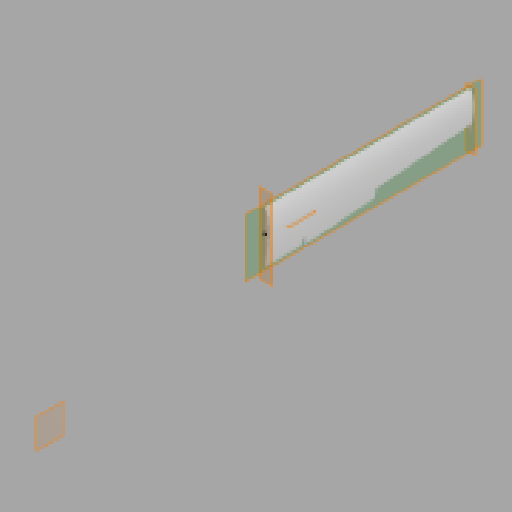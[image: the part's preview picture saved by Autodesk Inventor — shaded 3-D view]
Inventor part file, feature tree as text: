
AUTODESK INVENTOR PART (.ipt)
format: ipt  version: 2025 (Build 290162000, 162)  size: 286,208 bytes
history: native  units: in
note: dims shown in document units (in); Inventor stores cm internally (conversion verified against a paired STEP export)
features: other x7, plane x6, sketch x4
ambient origin geometry x8: Origin, YZ Plane, XZ Plane, XY Plane, X Axis, Y Axis, Z Axis, Center Point
bodies: Solid1 (feature_tree)
feature tree (17):
  other  "MiddleWingL.ipt"
  plane  "Work Plane7"
  plane  "Work Plane8"
  sketch  "Sketch8"  dims[d3=0.5in d4=0.0344in]
  other  "Solid1::MiddleWingL.ipt"
  other  "TaggingFeature1"
  sketch  "Sketch1"  dims[d0=0.3937in]
  sketch  "Sketch3"  dims[d1=0.5in]
  sketch  "Sketch4"  dims[d2=0.0344in]
  plane  "Work Plane1"
  plane  "Work Plane2"
  plane  "Work Plane3"
  plane  "Work Plane6"
  other  "UAV_Assembly_1.0.iam"
  other  "WingBox:1"
  other  "UAV_Assembly.iam"
  other  "Boom_MIR:1"
